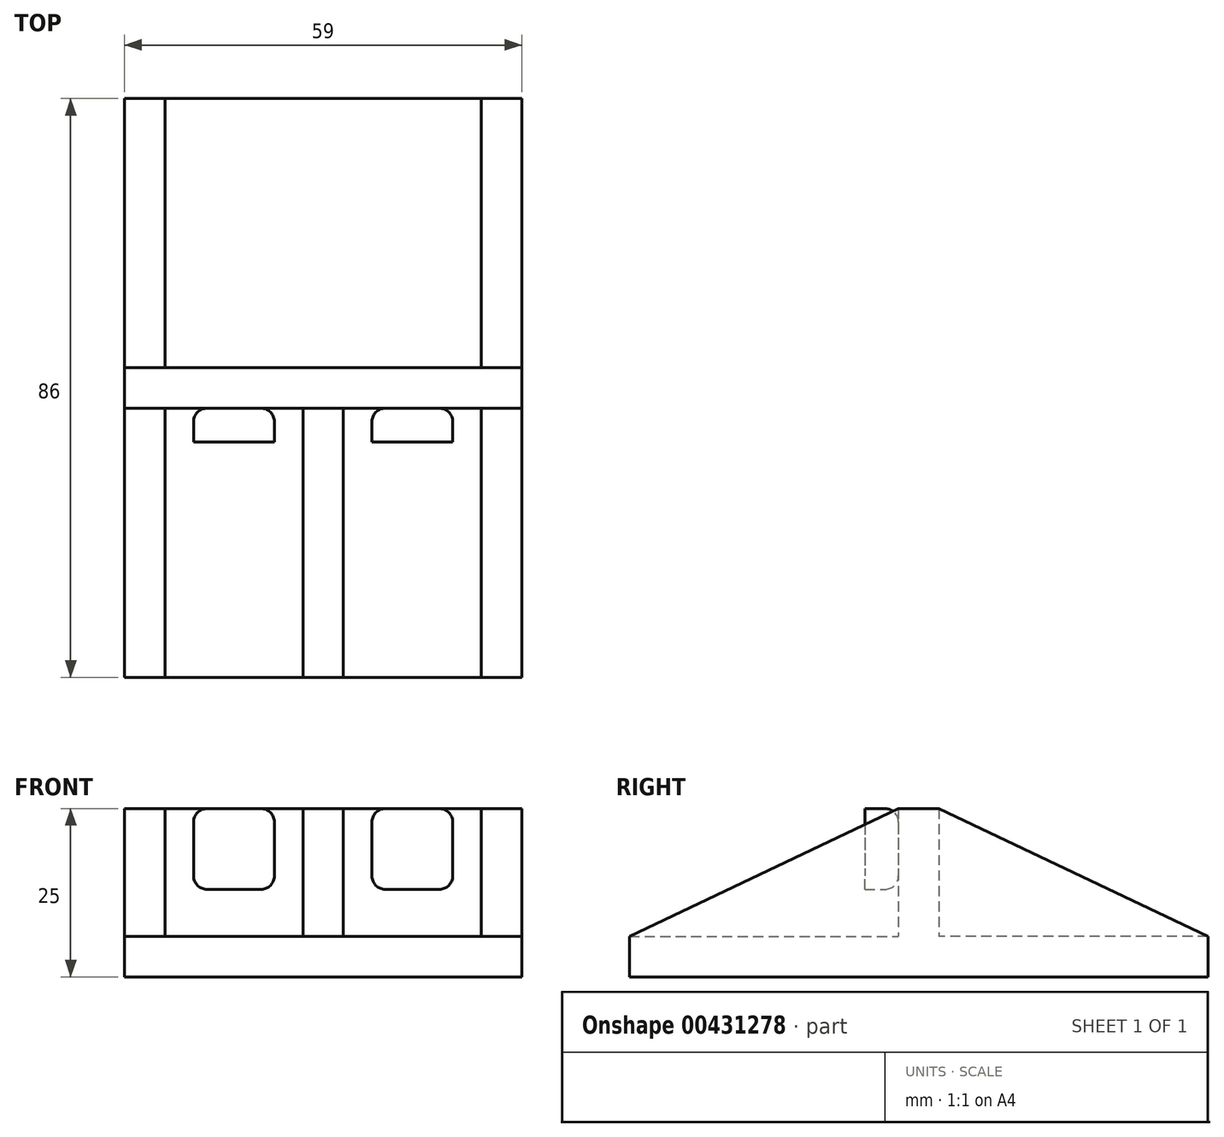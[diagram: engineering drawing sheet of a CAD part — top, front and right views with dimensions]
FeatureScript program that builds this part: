
annotation { "Feature Type Name" : "Feature", "Feature Type Description" : "" }
export const myFeature = defineFeature(function(context is Context, id is Id, definition is map)
    precondition{}
    {
        {
            var Q0;
            Q0=qCreatedBy(makeId("Top.planeOp"),FACE);
            var sketch = newSketch(context, id + "F0", { "sketchPlane" : qUnion([Q0])});
            skLineSegment(sketch, "E0.bottom", {"start": v(-29.5, 43) * mm, "end": v(29.5, 43) * mm});
            skLineSegment(sketch, "E0.top", {"start": v(-29.5, -43) * mm, "end": v(29.5, -43) * mm});
            skLineSegment(sketch, "E0.left", {"start": v(-29.5, 43) * mm, "end": v(-29.5, -43) * mm});
            skLineSegment(sketch, "E0.right", {"start": v(29.5, 43) * mm, "end": v(29.5, -43) * mm});
            skSolve(sketch);
        }
        {
            var Q0;
            Q0=makeQuery(id+"F0.imprint","IMPRINT",FACE,{"disambiguationData":[TD([[makeQuery(id+"F0.imprint","IMPRINT",EDGE,{"derivedFrom":sQuery(id+"F0.wireOp",EDGE,"E0.bottom")}),-1.0]])]});
            extrude(context, id + "F1", {"entities" : qUnion([Q0]), "depth" : 6 * mm});
        }
        {
            var Q0;
            Q0=makeQuery(id+"F1.opExtrude","CAP_FACE",FACE,{"disambiguationData":[OSD([sQuery(id+"F0.wireOp",EDGE,"E0.bottom"),sQuery(id+"F0.wireOp",EDGE,"E0.top"),sQuery(id+"F0.wireOp",EDGE,"E0.left"),sQuery(id+"F0.wireOp",EDGE,"E0.right")])],"isStart":false});
            var sketch = newSketch(context, id + "F2", { "sketchPlane" : qUnion([Q0])});
            skLineSegment(sketch, "E1.bottom", {"start": v(-29.5, 43) * mm, "end": v(-23.5, 43) * mm});
            skLineSegment(sketch, "E1.left", {"start": v(-29.5, 43) * mm, "end": v(-29.5, -43) * mm});
            skLineSegment(sketch, "E1.right", {"start": v(-23.5, 43) * mm, "end": v(-23.5, 3) * mm});
            skLineSegment(sketch, "E2.bottom", {"start": v(-23.5, 3) * mm, "end": v(23.5, 3) * mm});
            skLineSegment(sketch, "E2.top", {"start": v(-23.5, -3) * mm, "end": v(-3, -3) * mm});
            skLineSegment(sketch, "E2.right", {"start": v(29.5, 43) * mm, "end": v(29.5, -43) * mm});
            skLineSegment(sketch, "E3.bottom", {"start": v(-29.5, -43) * mm, "end": v(-23.5, -43) * mm});
            skLineSegment(sketch, "E3.right", {"start": v(-23.5, -43) * mm, "end": v(-23.5, -3) * mm});
            skLineSegment(sketch, "E4.bottom", {"start": v(29.5, -43) * mm, "end": v(23.5, -43) * mm});
            skLineSegment(sketch, "E4.right", {"start": v(23.5, -43) * mm, "end": v(23.5, -3) * mm});
            skLineSegment(sketch, "E5.bottom", {"start": v(29.5, 43) * mm, "end": v(23.5, 43) * mm});
            skLineSegment(sketch, "E5.right", {"start": v(23.5, 43) * mm, "end": v(23.5, 3) * mm});
            skLineSegment(sketch, "E6.bottom", {"start": v(3, -43) * mm, "end": v(-3, -43) * mm});
            skLineSegment(sketch, "E6.left", {"start": v(3, -43) * mm, "end": v(3, -3) * mm});
            skLineSegment(sketch, "E6.right", {"start": v(-3, -43) * mm, "end": v(-3, -3) * mm});
            skLineSegment(sketch, "E7.trimOffspring", {"start": v(3, -3) * mm, "end": v(23.5, -3) * mm});
            skPoint(sketch, "E8.orphan", {"position": v(29.5, -3) * mm});
            skSolve(sketch);
        }
        {
            var Q0;
            Q0=makeQuery(id+"F2.imprint","IMPRINT",FACE,{"disambiguationData":[TD([[makeQuery(id+"F2.imprint","IMPRINT",EDGE,{"derivedFrom":sQuery(id+"F2.wireOp",EDGE,"E1.bottom")}),-1.0]])]});
            extrude(context, id + "F3", {"entities" : qUnion([Q0]), "operationType" : NewBodyOperationType.ADD, "depth" : 19 * mm});
        }
        {
            var Q0;
            Q0=makeQuery(id+"F3.boolean.opBoolean","MERGE",FACE,{"derivedFrom":[makeQuery(id+"F1.opExtrude","SWEPT_FACE",FACE,{"disambiguationData":[OSD([sQuery(id+"F0.wireOp",EDGE,"E0.right")])]}),makeQuery(id+"F3.opExtrude","SWEPT_FACE",FACE,{"disambiguationData":[OSD([sQuery(id+"F2.wireOp",EDGE,"E2.right")])]})]});
            var sketch = newSketch(context, id + "F4", { "sketchPlane" : qUnion([Q0])});
            skLineSegment(sketch, "E9", {"start": v(-43, 6) * mm, "end": v(-3, 25) * mm});
            skLineSegment(sketch, "E10", {"start": v(-3, 25) * mm, "end": v(-43, 25) * mm});
            skLineSegment(sketch, "E11", {"start": v(-43, 25) * mm, "end": v(-43, 6) * mm});
            skLineSegment(sketch, "E12", {"start": v(43, 6) * mm, "end": v(3, 25) * mm});
            skLineSegment(sketch, "E13", {"start": v(3, 25) * mm, "end": v(43, 25) * mm});
            skLineSegment(sketch, "E14", {"start": v(43, 25) * mm, "end": v(43, 6) * mm});
            skSolve(sketch);
        }
        {
            var Q0;
            Q0=makeQuery(id+"F4.imprint","IMPRINT",FACE,{"disambiguationData":[TD([[makeQuery(id+"F4.imprint","IMPRINT",EDGE,{"derivedFrom":sQuery(id+"F4.wireOp",EDGE,"E9")}),1.0]])]});
            var Q1;
            Q1=makeQuery(id+"F4.imprint","IMPRINT",FACE,{"disambiguationData":[TD([[makeQuery(id+"F4.imprint","IMPRINT",EDGE,{"derivedFrom":sQuery(id+"F4.wireOp",EDGE,"E12")}),-1.0]])]});
            extrude(context, id + "F5", {"entities" : qUnion([Q0, Q1]), "operationType" : NewBodyOperationType.REMOVE, "endBound" : BoundingType.THROUGH_ALL, "oppositeDirection" : true, "depth" : 25 * mm});
        }
        {
            var Q0;
            Q0=makeQuery(id+"F3.opExtrude","SWEPT_FACE",FACE,{"disambiguationData":[OSD([sQuery(id+"F2.wireOp",EDGE,"E2.top")])]});
            var sketch = newSketch(context, id + "F6", { "sketchPlane" : qUnion([Q0])});
            skLineSegment(sketch, "E15.bottom", {"start": v(-19.25, 25) * mm, "end": v(-7.25, 25) * mm});
            skLineSegment(sketch, "E15.top", {"start": v(-19.25, 13) * mm, "end": v(-7.25, 13) * mm});
            skLineSegment(sketch, "E15.left", {"start": v(-19.25, 25) * mm, "end": v(-19.25, 13) * mm});
            skLineSegment(sketch, "E15.right", {"start": v(-7.25, 25) * mm, "end": v(-7.25, 13) * mm});
            skLineSegment(sketch, "E16.bottom", {"start": v(7.25, 25) * mm, "end": v(19.25, 25) * mm});
            skLineSegment(sketch, "E16.top", {"start": v(7.25, 13) * mm, "end": v(19.25, 13) * mm});
            skLineSegment(sketch, "E16.left", {"start": v(7.25, 25) * mm, "end": v(7.25, 13) * mm});
            skLineSegment(sketch, "E16.right", {"start": v(19.25, 25) * mm, "end": v(19.25, 13) * mm});
            skSolve(sketch);
        }
        {
            var Q0;
            Q0=makeQuery(id+"F6.imprint","IMPRINT",FACE,{"disambiguationData":[TD([[makeQuery(id+"F6.imprint","IMPRINT",EDGE,{"derivedFrom":sQuery(id+"F6.wireOp",EDGE,"E15.bottom")}),-1.0]])]});
            var Q1;
            Q1=makeQuery(id+"F6.imprint","IMPRINT",FACE,{"disambiguationData":[TD([[makeQuery(id+"F6.imprint","IMPRINT",EDGE,{"derivedFrom":sQuery(id+"F6.wireOp",EDGE,"E16.bottom")}),-1.0]])]});
            extrude(context, id + "F7", {"entities" : qUnion([Q0, Q1]), "depth" : 5 * mm});
        }
        {
            var Q0;
            Q0=makeQuery(id+"F7.opExtrude","CAP_EDGE",EDGE,{"disambiguationData":[OSD([sQuery(id+"F6.wireOp",EDGE,"E15.right")])],"isStart":true});
            var Q1;
            Q1=makeQuery(id+"F7.opExtrude","CAP_EDGE",EDGE,{"disambiguationData":[OSD([sQuery(id+"F6.wireOp",EDGE,"E15.bottom")])],"isStart":true});
            var Q2;
            Q2=makeQuery(id+"F7.opExtrude","CAP_EDGE",EDGE,{"disambiguationData":[OSD([sQuery(id+"F6.wireOp",EDGE,"E15.left")])],"isStart":true});
            var Q3;
            Q3=makeQuery(id+"F7.opExtrude","CAP_EDGE",EDGE,{"disambiguationData":[OSD([sQuery(id+"F6.wireOp",EDGE,"E15.top")])],"isStart":true});
            var Q4;
            Q4=makeQuery(id+"F7.opExtrude","CAP_EDGE",EDGE,{"disambiguationData":[OSD([sQuery(id+"F6.wireOp",EDGE,"E16.top")])],"isStart":true});
            var Q5;
            Q5=makeQuery(id+"F7.opExtrude","CAP_EDGE",EDGE,{"disambiguationData":[OSD([sQuery(id+"F6.wireOp",EDGE,"E16.left")])],"isStart":true});
            var Q6;
            Q6=makeQuery(id+"F7.opExtrude","CAP_EDGE",EDGE,{"disambiguationData":[OSD([sQuery(id+"F6.wireOp",EDGE,"E16.right")])],"isStart":true});
            var Q7;
            Q7=makeQuery(id+"F7.opExtrude","CAP_EDGE",EDGE,{"disambiguationData":[OSD([sQuery(id+"F6.wireOp",EDGE,"E16.bottom")])],"isStart":true});
            fillet(context, id + "F8", {"entities" : qUnion([Q0, Q1, Q2, Q3, Q4, Q5, Q6, Q7]), "radius" : 2 * mm, "tangentPropagation" : true, "allowEdgeOverflow" : false});
        }
        {
            var Q0;
            Q0=makeQuery(id+"F8.opFillet","BLEND_EDGE",EDGE,{"blendedFrom":[makeQuery(id+"F7.opExtrude","CAP_EDGE",EDGE,{"disambiguationData":[OSD([sQuery(id+"F6.wireOp",EDGE,"E15.bottom")])],"isStart":true}),makeQuery(id+"F7.opExtrude","CAP_EDGE",EDGE,{"disambiguationData":[OSD([sQuery(id+"F6.wireOp",EDGE,"E15.left")])],"isStart":true})],"blendedInto":[]});
            var Q1;
            Q1=makeQuery(id+"F8.opFillet","BLEND_EDGE",EDGE,{"blendedFrom":[makeQuery(id+"F7.opExtrude","CAP_EDGE",EDGE,{"disambiguationData":[OSD([sQuery(id+"F6.wireOp",EDGE,"E15.bottom")])],"isStart":true}),makeQuery(id+"F7.opExtrude","CAP_EDGE",EDGE,{"disambiguationData":[OSD([sQuery(id+"F6.wireOp",EDGE,"E15.right")])],"isStart":true})],"blendedInto":[]});
            var Q2;
            Q2=makeQuery(id+"F8.opFillet","BLEND_EDGE",EDGE,{"blendedFrom":[makeQuery(id+"F7.opExtrude","CAP_EDGE",EDGE,{"disambiguationData":[OSD([sQuery(id+"F6.wireOp",EDGE,"E15.top")])],"isStart":true}),makeQuery(id+"F7.opExtrude","CAP_EDGE",EDGE,{"disambiguationData":[OSD([sQuery(id+"F6.wireOp",EDGE,"E15.left")])],"isStart":true})],"blendedInto":[]});
            var Q3;
            Q3=makeQuery(id+"F8.opFillet","BLEND_EDGE",EDGE,{"blendedFrom":[makeQuery(id+"F7.opExtrude","CAP_EDGE",EDGE,{"disambiguationData":[OSD([sQuery(id+"F6.wireOp",EDGE,"E15.top")])],"isStart":true}),makeQuery(id+"F7.opExtrude","CAP_EDGE",EDGE,{"disambiguationData":[OSD([sQuery(id+"F6.wireOp",EDGE,"E15.right")])],"isStart":true})],"blendedInto":[]});
            var Q4;
            Q4=makeQuery(id+"F8.opFillet","BLEND_EDGE",EDGE,{"blendedFrom":[makeQuery(id+"F7.opExtrude","CAP_EDGE",EDGE,{"disambiguationData":[OSD([sQuery(id+"F6.wireOp",EDGE,"E16.bottom")])],"isStart":true}),makeQuery(id+"F7.opExtrude","CAP_EDGE",EDGE,{"disambiguationData":[OSD([sQuery(id+"F6.wireOp",EDGE,"E16.left")])],"isStart":true})],"blendedInto":[]});
            var Q5;
            Q5=makeQuery(id+"F8.opFillet","BLEND_EDGE",EDGE,{"blendedFrom":[makeQuery(id+"F7.opExtrude","CAP_EDGE",EDGE,{"disambiguationData":[OSD([sQuery(id+"F6.wireOp",EDGE,"E16.top")])],"isStart":true}),makeQuery(id+"F7.opExtrude","CAP_EDGE",EDGE,{"disambiguationData":[OSD([sQuery(id+"F6.wireOp",EDGE,"E16.left")])],"isStart":true})],"blendedInto":[]});
            var Q6;
            Q6=makeQuery(id+"F8.opFillet","BLEND_EDGE",EDGE,{"blendedFrom":[makeQuery(id+"F7.opExtrude","CAP_EDGE",EDGE,{"disambiguationData":[OSD([sQuery(id+"F6.wireOp",EDGE,"E16.bottom")])],"isStart":true}),makeQuery(id+"F7.opExtrude","CAP_EDGE",EDGE,{"disambiguationData":[OSD([sQuery(id+"F6.wireOp",EDGE,"E16.right")])],"isStart":true})],"blendedInto":[]});
            var Q7;
            Q7=makeQuery(id+"F8.opFillet","BLEND_EDGE",EDGE,{"blendedFrom":[makeQuery(id+"F7.opExtrude","CAP_EDGE",EDGE,{"disambiguationData":[OSD([sQuery(id+"F6.wireOp",EDGE,"E16.top")])],"isStart":true}),makeQuery(id+"F7.opExtrude","CAP_EDGE",EDGE,{"disambiguationData":[OSD([sQuery(id+"F6.wireOp",EDGE,"E16.right")])],"isStart":true})],"blendedInto":[]});
            fillet(context, id + "F9", {"entities" : qUnion([Q0, Q1, Q2, Q3, Q4, Q5, Q6, Q7]), "radius" : 2 * mm, "tangentPropagation" : true, "allowEdgeOverflow" : false});
        }
    });
